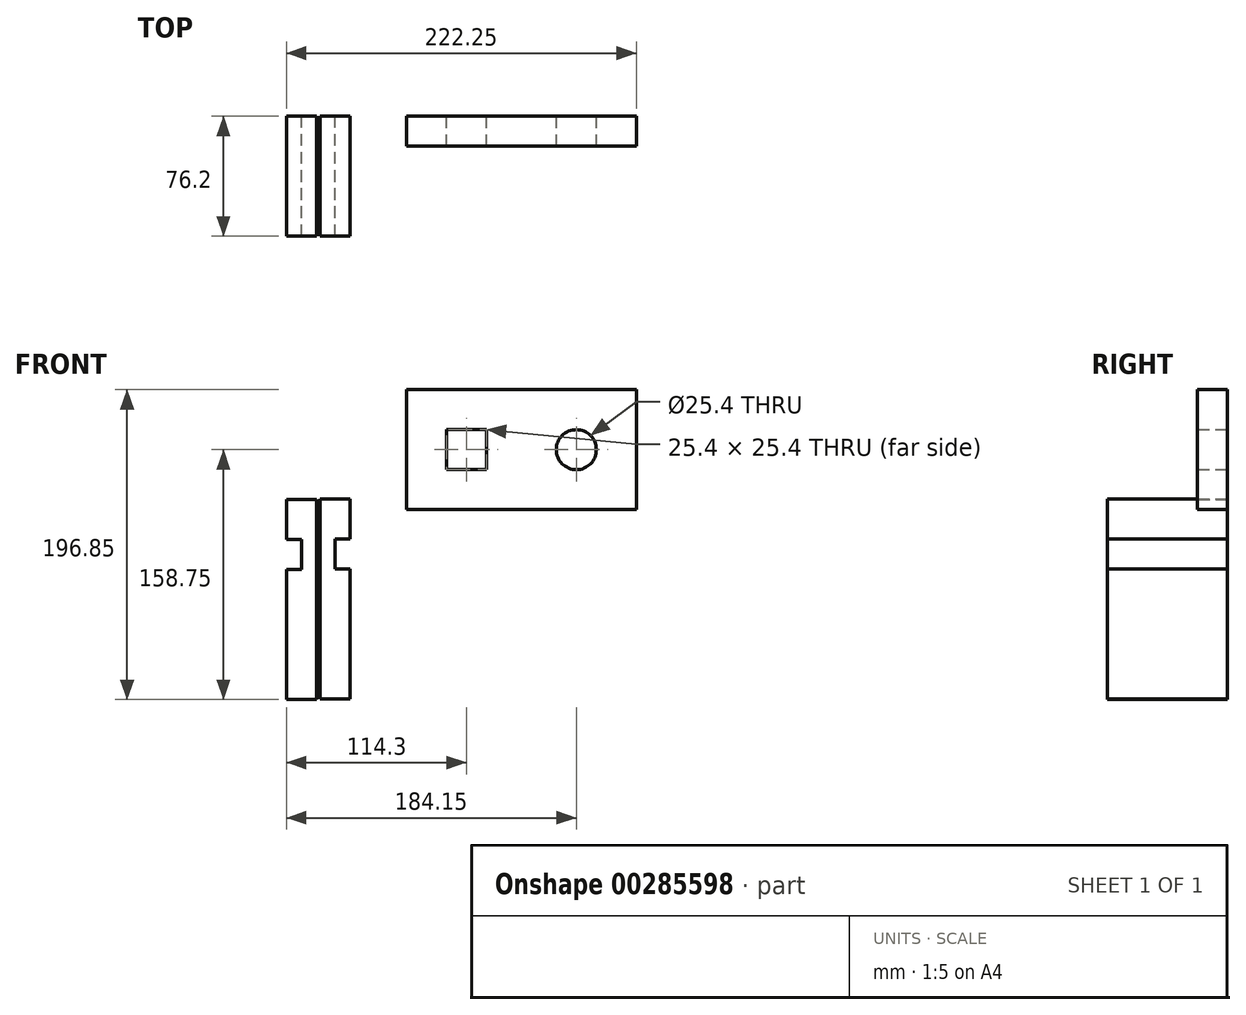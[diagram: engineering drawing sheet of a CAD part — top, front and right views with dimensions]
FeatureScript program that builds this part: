
annotation { "Feature Type Name" : "Feature", "Feature Type Description" : "" }
export const myFeature = defineFeature(function(context is Context, id is Id, definition is map)
    precondition{}
    {
        {
            var Q0;
            Q0=qCreatedBy(makeId("Front.planeOp"),FACE);
            var sketch = newSketch(context, id + "F0", { "sketchPlane" : qUnion([Q0])});
            skLineSegment(sketch, "E0", {"start": v(0, 0) * mm, "end": v(146.05, 0) * mm});
            skLineSegment(sketch, "E1", {"start": v(0, 0) * mm, "end": v(0, 76.2) * mm});
            skLineSegment(sketch, "E2", {"start": v(0, 76.2) * mm, "end": v(146.05, 76.2) * mm});
            skLineSegment(sketch, "E3", {"start": v(146.05, 76.2) * mm, "end": v(146.05, 0) * mm});
            skCircle(sketch, "E4", {"center": v(107.95, 38.1) * mm, "radius": 12.7 * mm});
            skLineSegment(sketch, "E5.bottom", {"start": v(25.4, 50.8) * mm, "end": v(50.8, 50.8) * mm});
            skLineSegment(sketch, "E5.top", {"start": v(25.4, 25.4) * mm, "end": v(50.8, 25.4) * mm});
            skLineSegment(sketch, "E5.left", {"start": v(25.4, 50.8) * mm, "end": v(25.4, 25.4) * mm});
            skLineSegment(sketch, "E5.right", {"start": v(50.8, 50.8) * mm, "end": v(50.8, 25.4) * mm});
            skSolve(sketch);
        }
        {
            var Q0;
            Q0 = qSketchRegion(id + "F0", true);
            extrude(context, id + "F1", {"entities" : qUnion([Q0]), "depth" : 19.05 * mm});
        }
        {
            var Q0;
            Q0=qCreatedBy(makeId("Front.planeOp"),FACE);
            var sketch = newSketch(context, id + "F2", { "sketchPlane" : qUnion([Q0])});
            skLineSegment(sketch, "E6", {"start": v(-76.2, -19.05) * mm, "end": v(-66.67, -19.05) * mm});
            skLineSegment(sketch, "E7", {"start": v(-66.67, -19.05) * mm, "end": v(-66.67, -38.1) * mm});
            skLineSegment(sketch, "E8", {"start": v(-66.67, -38.1) * mm, "end": v(-76.2, -38.1) * mm});
            skLineSegment(sketch, "E9", {"start": v(-76.2, -19.05) * mm, "end": v(-76.2, 6.35) * mm});
            skLineSegment(sketch, "E10", {"start": v(-76.2, 6.35) * mm, "end": v(-57.15, 6.35) * mm});
            skLineSegment(sketch, "E11", {"start": v(-57.15, 6.35) * mm, "end": v(-57.15, -120.65) * mm});
            skLineSegment(sketch, "E12", {"start": v(-57.15, -120.65) * mm, "end": v(-76.2, -120.65) * mm});
            skLineSegment(sketch, "E13", {"start": v(-76.2, -120.65) * mm, "end": v(-76.2, -38.1) * mm});
            skSolve(sketch);
        }
        {
            var Q0;
            Q0 = qSketchRegion(id + "F2", true);
            extrude(context, id + "F3", {"entities" : qUnion([Q0]), "depth" : 76.2 * mm});
        }
        {
            var Q0;
            Q0=qCreatedBy(makeId("Front.planeOp"),FACE);
            var sketch = newSketch(context, id + "F4", { "sketchPlane" : qUnion([Q0])});
            skLineSegment(sketch, "E14", {"start": v(-54.86, 6.86) * mm, "end": v(-35.8, 6.86) * mm});
            skLineSegment(sketch, "E15", {"start": v(-54.86, 6.86) * mm, "end": v(-54.86, -120.14) * mm});
            skLineSegment(sketch, "E16", {"start": v(-54.86, -120.14) * mm, "end": v(-35.8, -120.14) * mm});
            skLineSegment(sketch, "E17", {"start": v(-35.8, 6.86) * mm, "end": v(-35.8, -18.54) * mm});
            skLineSegment(sketch, "E18", {"start": v(-35.8, -18.54) * mm, "end": v(-45.33, -18.54) * mm});
            skLineSegment(sketch, "E19", {"start": v(-45.33, -18.54) * mm, "end": v(-45.33, -37.6) * mm});
            skLineSegment(sketch, "E20", {"start": v(-45.33, -37.6) * mm, "end": v(-35.8, -37.6) * mm});
            skLineSegment(sketch, "E21", {"start": v(-35.8, -37.6) * mm, "end": v(-35.8, -120.14) * mm});
            skSolve(sketch);
        }
        {
            var Q0;
            Q0 = qSketchRegion(id + "F4", true);
            extrude(context, id + "F5", {"entities" : qUnion([Q0]), "depth" : 76.2 * mm});
        }
    });
